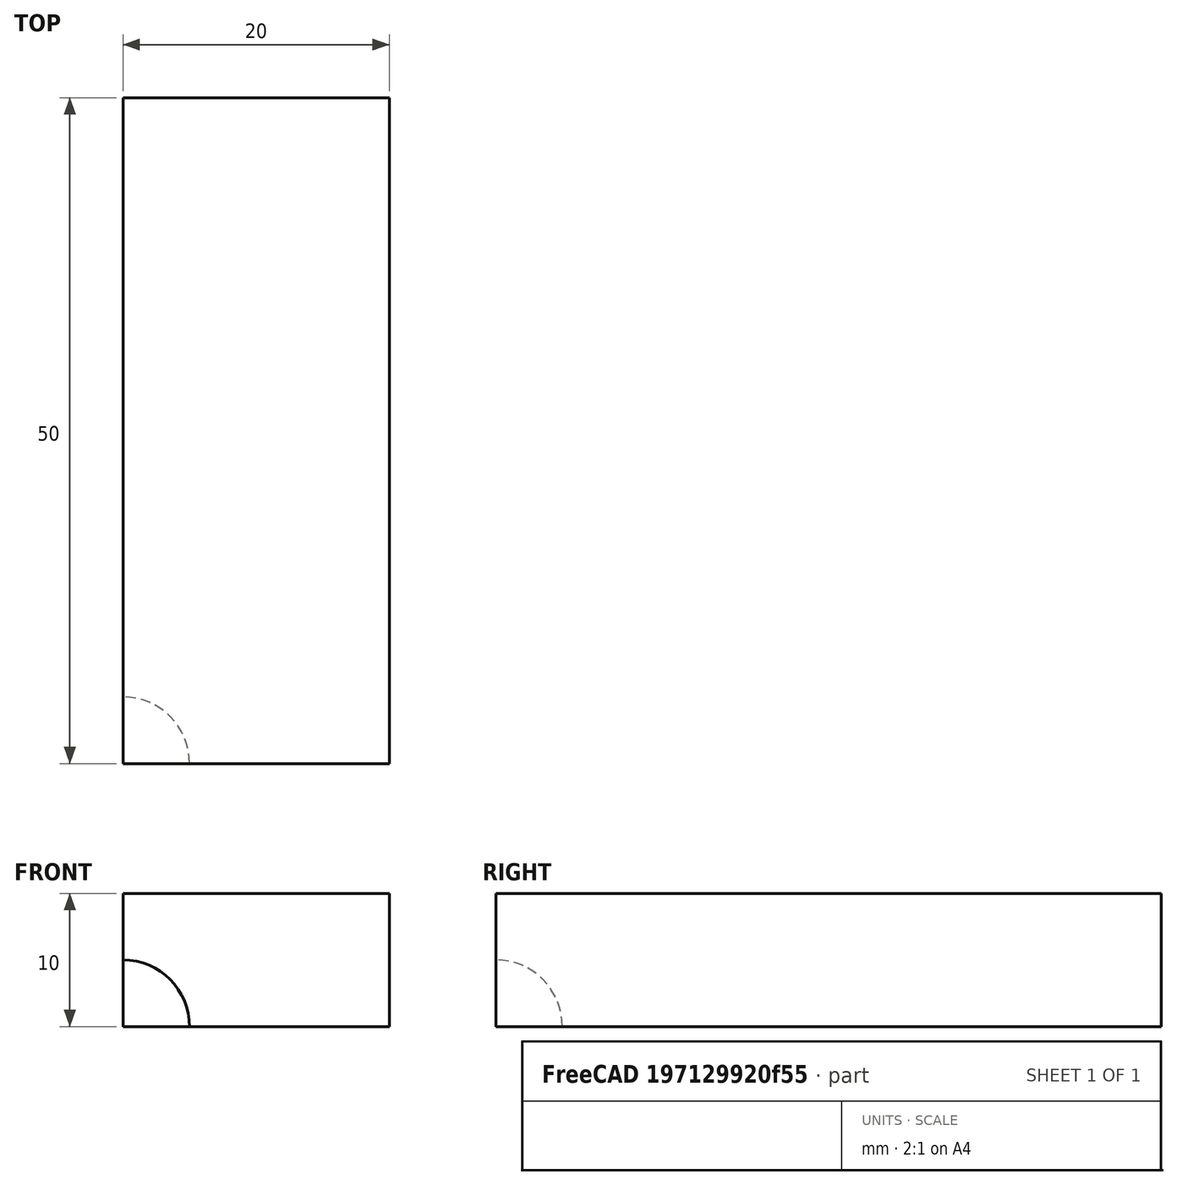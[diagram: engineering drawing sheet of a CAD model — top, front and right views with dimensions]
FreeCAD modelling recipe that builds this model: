
FCSTD DOCUMENT  (FreeCAD 0.20R29410 (Git))
Label: Spreadsheet_Workflow
License: All rights reserved
LicenseURL: http://en.wikipedia.org/wiki/All_rights_reserved
objects: Part::Box×1, Spreadsheet::Sheet×1, Part::Sphere×1, App::Part×1, Part::Cut×1
note: 3 computed .brp shape members not serialized (recipe doc carries the construction recipe); baked Part::Feature solids carry a one-line shape summary decoded from their .brp

FEATURE [Part::Box] Box  label="Cube"
  AttacherType = Attacher::AttachEngine3D
  Height = 10
  Length = 20
  Width = 50
  expr: Height = Spreadsheet.Height
  expr: Length = Spreadsheet.Length
  expr: Width = Spreadsheet.Width
FEATURE [Spreadsheet::Sheet] Spreadsheet
  Configurations = 3
  cells = B1=Height; C1=Width; D1=Length; A2==hiddenref(Part.Configurations.String); B2(Height)==.B6; C2(Width)==.C6; D2(Length)==.D6; A3=1x1x1; B3=10; C3=10; D3=10; A4=1x1x2; B4=10; C4=10; D4=20; A5=2x2x2; B5=20; C5=20; D5=20; A6=1x5x2; B6=10; C6=50; D6=20; A7=1x2x2; B7=10; C7=20; D7=20
  expr: .Configurations.Enum = cells[<<A3:|>>]
  expr: .cells.Bind.B2.ZZ2 = tuple(.cells; <<B>> + str(hiddenref(Part.Configurations) + 3); <<ZZ>> + str(hiddenref(Part.Configurations) + 3))
FEATURE [Part::Sphere] Sphere
  Angle1 = -90
  Angle2 = 90
  Angle3 = 360
  AttacherType = Attacher::AttachEngine3D
  Radius = 5
FEATURE [App::Part] Part
  Configurations = 3
  Group = -> [Box,Sphere]
  Origin = -> Origin
  expr: .Configurations.Enum = Spreadsheet.cells[<<A3:|>>]
FEATURE [Part::Cut] Cut
  Base = -> Box
  Tool = -> Sphere
